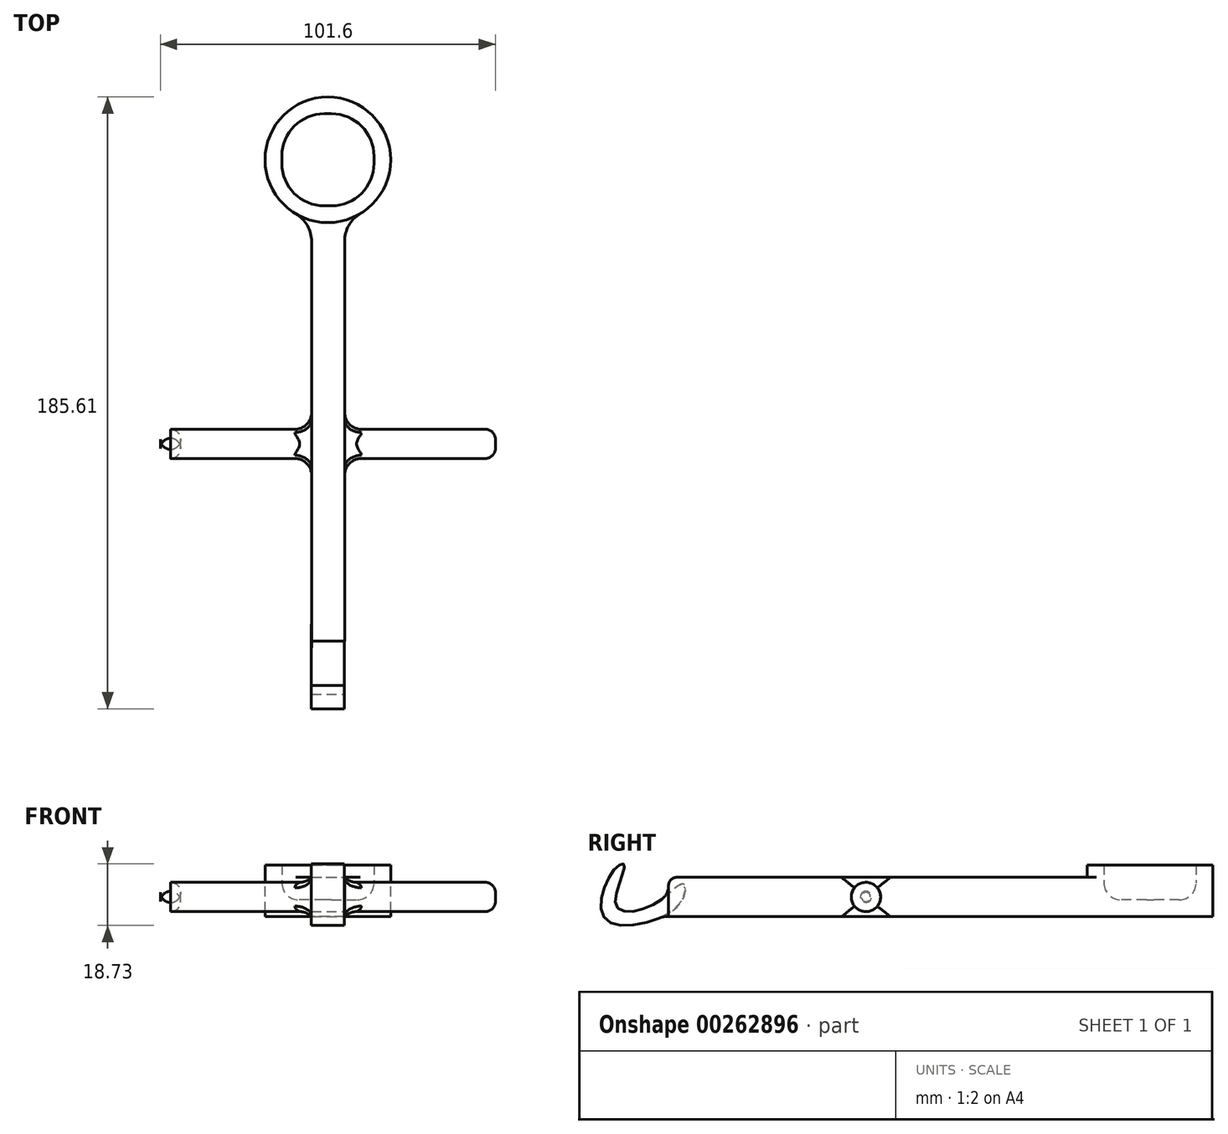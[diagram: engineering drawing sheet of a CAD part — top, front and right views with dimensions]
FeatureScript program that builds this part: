
annotation { "Feature Type Name" : "Feature", "Feature Type Description" : "" }
export const myFeature = defineFeature(function(context is Context, id is Id, definition is map)
    precondition{}
    {
        {
            var Q0;
            Q0=qCreatedBy(makeId("Top.planeOp"),FACE);
            var sketch = newSketch(context, id + "F0", { "sketchPlane" : qUnion([Q0])});
            skLineSegment(sketch, "E0.bottom", {"start": v(19.05, -19.05) * mm, "end": v(-19.05, -19.05) * mm});
            skLineSegment(sketch, "E0.top", {"start": v(19.05, 19.05) * mm, "end": v(-19.05, 19.05) * mm});
            skLineSegment(sketch, "E0.left", {"start": v(19.05, -19.05) * mm, "end": v(19.05, 19.05) * mm});
            skLineSegment(sketch, "E0.right", {"start": v(-19.05, -19.05) * mm, "end": v(-19.05, 19.05) * mm});
            skPoint(sketch, "E0.middle", {"position": v(0, 0) * mm});
            skLineSegment(sketch, "E1", {"start": v(-4.93, -19.05) * mm, "end": v(-4.93, -146.05) * mm});
            skLineSegment(sketch, "E2", {"start": v(-4.93, -146.05) * mm, "end": v(5.07, -146.05) * mm});
            skLineSegment(sketch, "E3", {"start": v(5.07, -146.05) * mm, "end": v(5.07, -19.05) * mm});
            skSolve(sketch);
        }
        {
            var Q0;
            {var subQ0=sQuery(id+"F0.wireOp",EDGE,"E1");Q0=makeQuery(id+"F0.imprint","IMPRINT",FACE,{"disambiguationData":[TD([[makeQuery(id+"F0.imprint","IMPRINT",EDGE,{"derivedFrom":subQ0}),1.0]])]});}
            extrude(context, id + "F1", {"entities" : qUnion([Q0]), "depth" : 11.94 * mm});
        }
        {
            var Q0;
            Q0=makeQuery(id+"F0.imprint","IMPRINT",FACE,{"disambiguationData":[TD([[makeQuery(id+"F0.imprint","IMPRINT",EDGE,{"derivedFrom":sQuery(id+"F0.wireOp",EDGE,"E0.top")}),1.0]])]});
            extrude(context, id + "F2", {"entities" : qUnion([Q0]), "operationType" : NewBodyOperationType.ADD, "depth" : 25.4 * mm});
        }
        {
            var Q0;
            Q0=makeQuery(id+"F2.opExtrude","CAP_FACE",FACE,{"disambiguationData":[OSD([sQuery(id+"F0.wireOp",EDGE,"E0.bottom"),sQuery(id+"F0.wireOp",EDGE,"E0.top"),sQuery(id+"F0.wireOp",EDGE,"E0.left"),sQuery(id+"F0.wireOp",EDGE,"E0.right")])],"isStart":false});
            shell(context, id + "F3", {"entities" : qUnion([Q0]), "thickness" : 5.08 * mm});
        }
        {
            var Q0;
            Q0=qCreatedBy(makeId("Right.planeOp"),FACE);
            var sketch = newSketch(context, id + "F4", { "sketchPlane" : qUnion([Q0])});
            skCircle(sketch, "E4", {"center": v(-86.18, 5.98) * mm, "radius": 4.45 * mm});
            skSolve(sketch);
        }
        {
            var Q0;
            Q0 = qSketchRegion(id + "F4", true);
            extrude(context, id + "F5", {"entities" : qUnion([Q0]), "operationType" : NewBodyOperationType.ADD, "endBound" : BoundingType.SYMMETRIC, "depth" : 101.6 * mm});
        }
        {
            var Q0;
            Q0=makeQuery(id+"F3.opShell","OFFSET_EDGE",EDGE,{"disambiguationData":[OSD([sQuery(id+"F0.wireOp",EDGE,"E0.bottom"),sQuery(id+"F0.wireOp",EDGE,"E0.right")])]});
            var Q1;
            Q1=makeQuery(id+"F3.opShell","OFFSET_EDGE",EDGE,{"disambiguationData":[OSD([sQuery(id+"F0.wireOp",EDGE,"E0.bottom"),sQuery(id+"F0.wireOp",EDGE,"E0.left")])]});
            var Q2;
            Q2=makeQuery(id+"F3.opShell","OFFSET_EDGE",EDGE,{"disambiguationData":[OSD([sQuery(id+"F0.wireOp",EDGE,"E0.top"),sQuery(id+"F0.wireOp",EDGE,"E0.left")])]});
            var Q3;
            Q3=makeQuery(id+"F3.opShell","OFFSET_EDGE",EDGE,{"disambiguationData":[OSD([sQuery(id+"F0.wireOp",EDGE,"E0.top"),sQuery(id+"F0.wireOp",EDGE,"E0.right")])]});
            fillet(context, id + "F6", {"entities" : qUnion([Q0, Q1, Q2, Q3]), "radius" : 12.88 * mm, "tangentPropagation" : true, "allowEdgeOverflow" : false});
        }
        {
            var Q0;
            Q0=makeQuery(id+"F2.opExtrude","SWEPT_EDGE",EDGE,{"disambiguationData":[OSD([sQuery(id+"F0.wireOp",EDGE,"E0.bottom"),sQuery(id+"F0.wireOp",EDGE,"E0.right")])]});
            var Q1;
            Q1=makeQuery(id+"F2.opExtrude","SWEPT_EDGE",EDGE,{"disambiguationData":[OSD([sQuery(id+"F0.wireOp",EDGE,"E0.top"),sQuery(id+"F0.wireOp",EDGE,"E0.right")])]});
            var Q2;
            Q2=makeQuery(id+"F2.opExtrude","SWEPT_EDGE",EDGE,{"disambiguationData":[OSD([sQuery(id+"F0.wireOp",EDGE,"E0.top"),sQuery(id+"F0.wireOp",EDGE,"E0.left")])]});
            var Q3;
            Q3=makeQuery(id+"F2.opExtrude","SWEPT_EDGE",EDGE,{"disambiguationData":[OSD([sQuery(id+"F0.wireOp",EDGE,"E0.bottom"),sQuery(id+"F0.wireOp",EDGE,"E0.left")])]});
            fillet(context, id + "F7", {"entities" : qUnion([Q0, Q1, Q2, Q3]), "radius" : 19.05 * mm, "tangentPropagation" : true, "allowEdgeOverflow" : false});
        }
        {
            var Q0;
            Q0=makeQuery(id+"F2.opExtrude","CAP_FACE",FACE,{"disambiguationData":[OSD([sQuery(id+"F0.wireOp",EDGE,"E0.bottom"),sQuery(id+"F0.wireOp",EDGE,"E0.top"),sQuery(id+"F0.wireOp",EDGE,"E0.left"),sQuery(id+"F0.wireOp",EDGE,"E0.right")])],"isStart":false});
            extrude(context, id + "F8", {"entities" : qUnion([Q0]), "operationType" : NewBodyOperationType.REMOVE, "oppositeDirection" : true, "depth" : 3.86 * mm});
        }
        {
            var Q0;
            Q0=makeQuery(id+"F5.boolean.opBoolean","INTERSECT",EDGE,{"derivedFrom":[makeQuery(id+"F1.opExtrude","SWEPT_FACE",FACE,{"disambiguationData":[OSD([sQuery(id+"F0.wireOp",EDGE,"E3")])]}),makeQuery(id+"F5.opExtrude","SWEPT_FACE",FACE,{"disambiguationData":[OSD([sQuery(id+"F4.wireOp",EDGE,"E4")])]})]});
            var Q1;
            Q1=makeQuery(id+"F5.boolean.opBoolean","INTERSECT",EDGE,{"derivedFrom":[makeQuery(id+"F1.opExtrude","SWEPT_FACE",FACE,{"disambiguationData":[OSD([sQuery(id+"F0.wireOp",EDGE,"E1")])]}),makeQuery(id+"F5.opExtrude","SWEPT_FACE",FACE,{"disambiguationData":[OSD([sQuery(id+"F4.wireOp",EDGE,"E4")])]})]});
            fillet(context, id + "F9", {"entities" : qUnion([Q0, Q1]), "radius" : 5.08 * mm, "tangentPropagation" : true, "allowEdgeOverflow" : false});
        }
        {
            var Q0;
            {var subQ0=sQuery(id+"F0.wireOp",EDGE,"E0.right");var subQ1=sQuery(id+"F0.wireOp",EDGE,"E0.bottom");Q0=makeQuery(id+"F6.opFillet","BLEND_EDGE",EDGE,{"blendedFrom":[makeQuery(id+"F3.opShell","OFFSET_EDGE",EDGE,{"disambiguationData":[OSD([subQ1,subQ0])]}),makeQuery(id+"F3.opShell","OFFSET_FACE",FACE,{"disambiguationData":[OSD([subQ1,sQuery(id+"F0.wireOp",EDGE,"E0.top"),sQuery(id+"F0.wireOp",EDGE,"E0.left"),subQ0,sQuery(id+"F0.wireOp",EDGE,"E1"),sQuery(id+"F0.wireOp",EDGE,"E2"),sQuery(id+"F0.wireOp",EDGE,"E3")])]})],"blendedInto":[makeQuery(id+"F3.opShell","OFFSET_FACE",FACE,{"disambiguationData":[OSD([subQ1,sQuery(id+"F0.wireOp",EDGE,"E0.top"),sQuery(id+"F0.wireOp",EDGE,"E0.left"),subQ0,sQuery(id+"F0.wireOp",EDGE,"E1"),sQuery(id+"F0.wireOp",EDGE,"E2"),sQuery(id+"F0.wireOp",EDGE,"E3")])]})]});}
            fillet(context, id + "F10", {"entities" : qUnion([Q0]), "radius" : 5.08 * mm, "tangentPropagation" : true, "allowEdgeOverflow" : false});
        }
        {
            var Q0;
            Q0=qCreatedBy(makeId("Right.planeOp"),FACE);
            var sketch = newSketch(context, id + "F11", { "sketchPlane" : qUnion([Q0])});
            skFitSpline(sketch, "E5", {"points": [v(-141.58, 9.9) * mm, v(-150.28, 3.85) * mm, v(-161.97, 3.49) * mm, v(-159.45, 15.6) * mm, v(-162.3, 14.57) * mm, v(-165.12, -0.77) * mm, v(-143.04, 3.37) * mm, v(-141.58, 9.9) * mm]});
            skSolve(sketch);
        }
        {
            var Q0;
            Q0=makeQuery(id+"F11.imprint","IMPRINT",FACE,{"disambiguationData":[TD([[makeQuery(id+"F11.imprint","IMPRINT",EDGE,{"derivedFrom":sQuery(id+"F11.wireOp",EDGE,"E5")}),1.0]])]});
            extrude(context, id + "F12", {"entities" : qUnion([Q0]), "operationType" : NewBodyOperationType.ADD, "endBound" : BoundingType.SYMMETRIC, "depth" : 10 * mm});
        }
        {
            var Q0;
            Q0=makeQuery(id+"F12.boolean.opBoolean","INTERSECT",EDGE,{"disambiguationData":[OD(1.0)],"derivedFrom":[makeQuery(id+"F1.opExtrude","SWEPT_FACE",FACE,{"disambiguationData":[OSD([sQuery(id+"F0.wireOp",EDGE,"E2")])]}),makeQuery(id+"F12.opExtrude","SWEPT_FACE",FACE,{"disambiguationData":[OSD([sQuery(id+"F11.wireOp",EDGE,"E5")])]})]});
            fillet(context, id + "F13", {"entities" : qUnion([Q0]), "radius" : 5 * mm, "tangentPropagation" : true, "allowEdgeOverflow" : false});
        }
        {
            var Q0;
            Q0=makeQuery(id+"F1.opExtrude","CAP_EDGE",EDGE,{"disambiguationData":[OSD([sQuery(id+"F0.wireOp",EDGE,"E2")])],"isStart":false});
            fillet(context, id + "F14", {"entities" : qUnion([Q0]), "radius" : 2.45 * mm, "tangentPropagation" : true, "allowEdgeOverflow" : false});
        }
        {
            var Q0;
            Q0=makeQuery(id+"F12.boolean.opBoolean","INTERSECT",EDGE,{"disambiguationData":[OD(0.0)],"derivedFrom":[makeQuery(id+"F1.opExtrude","SWEPT_FACE",FACE,{"disambiguationData":[OSD([sQuery(id+"F0.wireOp",EDGE,"E2")])]}),makeQuery(id+"F12.opExtrude","SWEPT_FACE",FACE,{"disambiguationData":[OSD([sQuery(id+"F11.wireOp",EDGE,"E5")])]})]});
            fillet(context, id + "F15", {"entities" : qUnion([Q0]), "radius" : 5.55 * mm, "tangentPropagation" : true, "allowEdgeOverflow" : false});
        }
        {
            var Q0;
            Q0=makeQuery(id+"F5.opExtrude","CAP_EDGE",EDGE,{"disambiguationData":[OSD([sQuery(id+"F4.wireOp",EDGE,"E4")])],"isStart":true});
            var Q1;
            Q1=makeQuery(id+"F5.opExtrude","CAP_EDGE",EDGE,{"disambiguationData":[OSD([sQuery(id+"F4.wireOp",EDGE,"E4")])],"isStart":false});
            fillet(context, id + "F16", {"entities" : qUnion([Q0, Q1]), "radius" : 3.07 * mm, "tangentPropagation" : true, "allowEdgeOverflow" : false});
        }
        {
            var Q0;
            Q0=makeQuery(id+"F8.boolean.opBoolean","COPY",FACE,{"derivedFrom":makeQuery(id+"F8.opExtrude","CAP_FACE",FACE,{"disambiguationData":[OSD([sQuery(id+"F0.wireOp",EDGE,"E0.bottom"),sQuery(id+"F0.wireOp",EDGE,"E0.top"),sQuery(id+"F0.wireOp",EDGE,"E0.left"),sQuery(id+"F0.wireOp",EDGE,"E0.right")])],"isStart":false})});
            extrude(context, id + "F17", {"entities" : qUnion([Q0]), "operationType" : NewBodyOperationType.REMOVE, "oppositeDirection" : true, "depth" : 5.84 * mm});
        }
        {
            var Q0;
            Q0=makeQuery(id+"F7.opFillet","BLEND_EDGE",EDGE,{"blendedFrom":[makeQuery(id+"F2.opExtrude","SWEPT_EDGE",EDGE,{"disambiguationData":[OSD([sQuery(id+"F0.wireOp",EDGE,"E0.bottom"),sQuery(id+"F0.wireOp",EDGE,"E0.left")])]}),makeQuery(id+"F1.opExtrude","SWEPT_FACE",FACE,{"disambiguationData":[OSD([sQuery(id+"F0.wireOp",EDGE,"E3")])]})],"blendedInto":[makeQuery(id+"F1.opExtrude","SWEPT_FACE",FACE,{"disambiguationData":[OSD([sQuery(id+"F0.wireOp",EDGE,"E3")])]})]});
            var Q1;
            Q1=makeQuery(id+"F7.opFillet","BLEND_EDGE",EDGE,{"blendedFrom":[makeQuery(id+"F2.opExtrude","SWEPT_EDGE",EDGE,{"disambiguationData":[OSD([sQuery(id+"F0.wireOp",EDGE,"E0.bottom"),sQuery(id+"F0.wireOp",EDGE,"E0.right")])]}),makeQuery(id+"F1.opExtrude","SWEPT_FACE",FACE,{"disambiguationData":[OSD([sQuery(id+"F0.wireOp",EDGE,"E1")])]})],"blendedInto":[makeQuery(id+"F1.opExtrude","SWEPT_FACE",FACE,{"disambiguationData":[OSD([sQuery(id+"F0.wireOp",EDGE,"E1")])]})]});
            fillet(context, id + "F18", {"entities" : qUnion([Q0, Q1]), "radius" : 9.84 * mm, "tangentPropagation" : true, "allowEdgeOverflow" : false});
        }
    });
